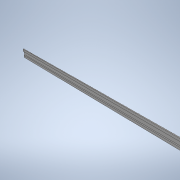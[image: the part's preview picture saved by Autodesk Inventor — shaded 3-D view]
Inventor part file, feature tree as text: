
AUTODESK INVENTOR PART (.ipt)
format: ipt  version: 2020.3 (Build 243373000, 373)  size: 291,840 bytes
history: native  units: mm (DEFAULTED — no unit token found)
features: extrude x2, sketch x2, pattern_linear x1
ambient origin geometry x8: Origin, YZ Plane, XZ Plane, XY Plane, X Axis, Y Axis, Z Axis, Center Point
bodies: Solid1 (feature_tree)
feature tree (5):
  extrude  "Extrusion1"  Depth=5.0mm TaperAngle=0.0deg
  extrude  "Extrusion2"  [1 undecoded]
  pattern_linear  "Rectangular Pattern1"  [2 undecoded]
  sketch  "Sketch_1"  dims[d0=200.0mm d1=0.0mm d2=5.0mm d3=0.0mm]
  sketch  "Sketch_5"  dims[d4=6410.0mm d6=3.14159mm d7=10.0mm d9=0.0mm]
note: 3 required parameter values undecoded (feature->parameter linkage not recoverable at this tier; creation-order binding heuristic only, values carry confidence <= 0.55)
